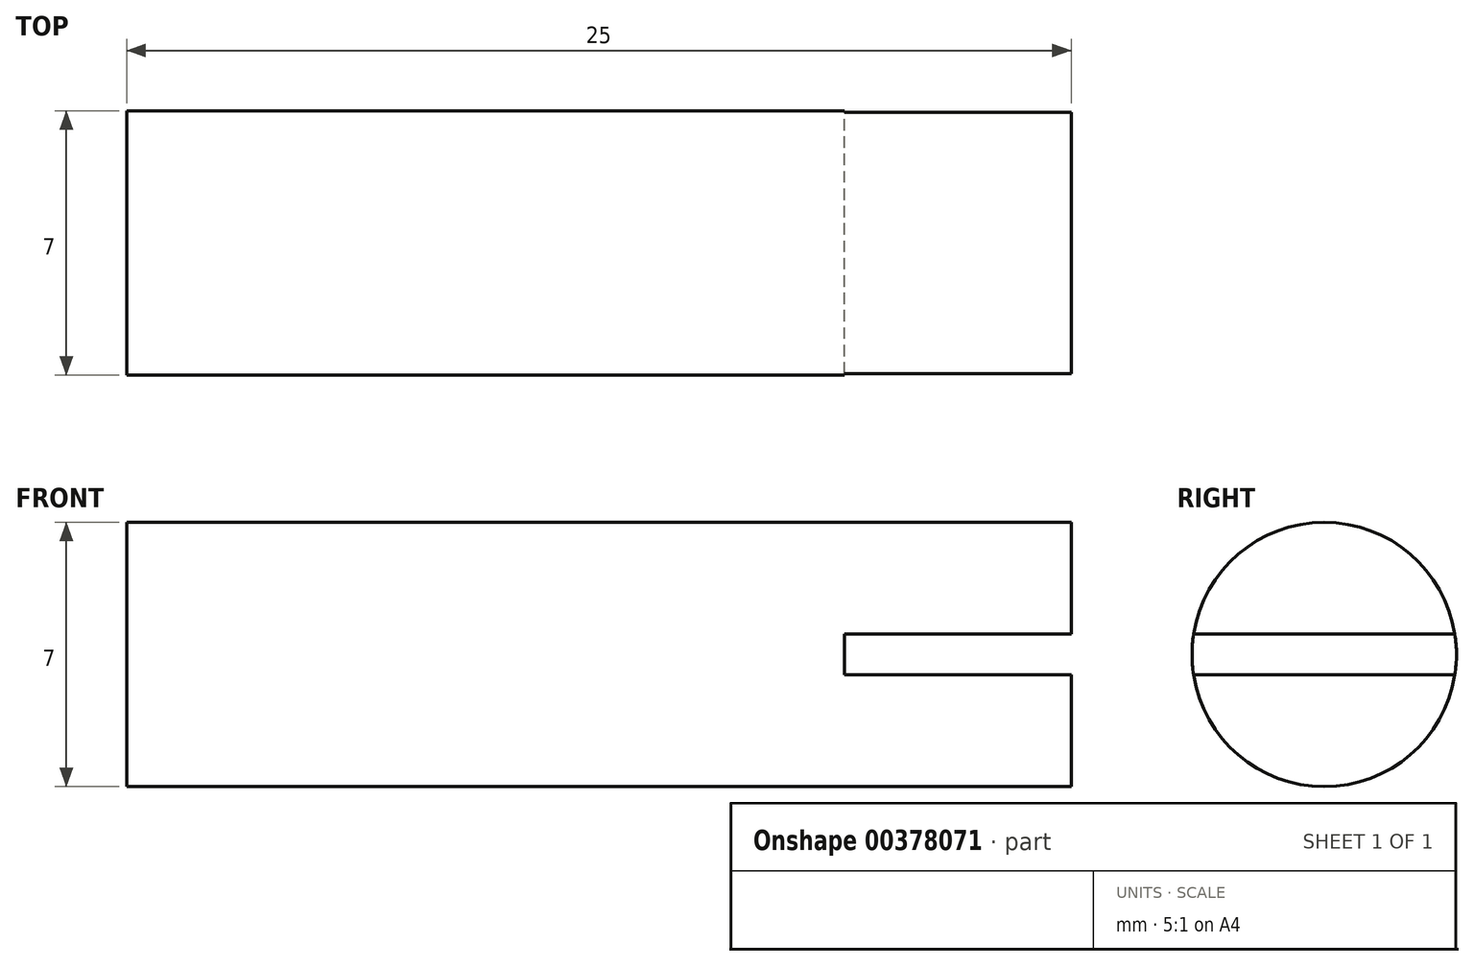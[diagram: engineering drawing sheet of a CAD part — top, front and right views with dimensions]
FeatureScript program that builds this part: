
annotation { "Feature Type Name" : "Feature", "Feature Type Description" : "" }
export const myFeature = defineFeature(function(context is Context, id is Id, definition is map)
    precondition{}
    {
        {
            var Q0;
            Q0=qCreatedBy(makeId("Front.planeOp"),FACE);
            var sketch = newSketch(context, id + "F0", { "sketchPlane" : qUnion([Q0])});
            skLineSegment(sketch, "E0.bottom", {"start": v(0, 3.5) * mm, "end": v(25, 3.5) * mm});
            skLineSegment(sketch, "E0.top", {"start": v(0, 0) * mm, "end": v(25, 0) * mm});
            skLineSegment(sketch, "E0.left", {"start": v(0, 3.5) * mm, "end": v(0, 0) * mm});
            skLineSegment(sketch, "E0.right", {"start": v(25, 3.5) * mm, "end": v(25, 0) * mm});
            skSolve(sketch);
        }
        {
            var Q0;
            Q0=makeQuery(id+"F0.imprint","IMPRINT",FACE,{"disambiguationData":[TD([[makeQuery(id+"F0.imprint","IMPRINT",EDGE,{"derivedFrom":sQuery(id+"F0.wireOp",EDGE,"E0.bottom")}),-1.0]])]});
            var Q1;
            Q1=sQuery(id+"F0.wireOp",EDGE,"E0.top");
            revolve(context, id + "F1", {"entities" : qUnion([Q0]), "axis" : qUnion([Q1]), "revolveType" : RevolveType.FULL});
        }
        {
            var Q0;
            Q0=makeQuery(id+"F1.opRevolve","SWEPT_FACE",FACE,{"disambiguationData":[OSD([sQuery(id+"F0.wireOp",EDGE,"E0.right")])]});
            var sketch = newSketch(context, id + "F2", { "sketchPlane" : qUnion([Q0])});
            skArc(sketch, "E1", {"start": v(3.5, -0.54) * mm, "mid": v(3.55, 0) * mm, "end": v(3.5, 0.54) * mm});
            skLineSegment(sketch, "E2", {"start": v(-3.5, 0.54) * mm, "end": v(3.5, 0.54) * mm});
            skLineSegment(sketch, "E3", {"start": v(-3.5, -0.54) * mm, "end": v(3.5, -0.54) * mm});
            skArc(sketch, "E4.trimOffspring", {"start": v(-3.5, 0.54) * mm, "mid": v(-3.55, 0) * mm, "end": v(-3.5, -0.54) * mm});
            skSolve(sketch);
        }
        {
            var Q0;
            {var subQ0=sQuery(id+"F2.wireOp",EDGE,"E2");var subQ1=makeQuery(id+"F1.opRevolve","SWEPT_EDGE",EDGE,{"disambiguationData":[OSD([sQuery(id+"F0.wireOp",EDGE,"E0.bottom"),sQuery(id+"F0.wireOp",EDGE,"E0.right")])]});var subQ2=makeQuery(id+"F2.imprint","INTERSECT",VERTEX,{"disambiguationData":[OD(0.0)],"derivedFrom":[subQ1,subQ0]});Q0=makeQuery(id+"F2.imprint","IMPRINT",FACE,{"disambiguationData":[TD([[makeQuery(id+"F2.imprint","IMPRINT",EDGE,{"disambiguationData":[TD([[subQ2,-1.0]])],"derivedFrom":subQ0}),-1.0]])]});}
            extrude(context, id + "F3", {"entities" : qUnion([Q0]), "operationType" : NewBodyOperationType.REMOVE, "oppositeDirection" : true, "depth" : 6 * mm});
        }
    });
